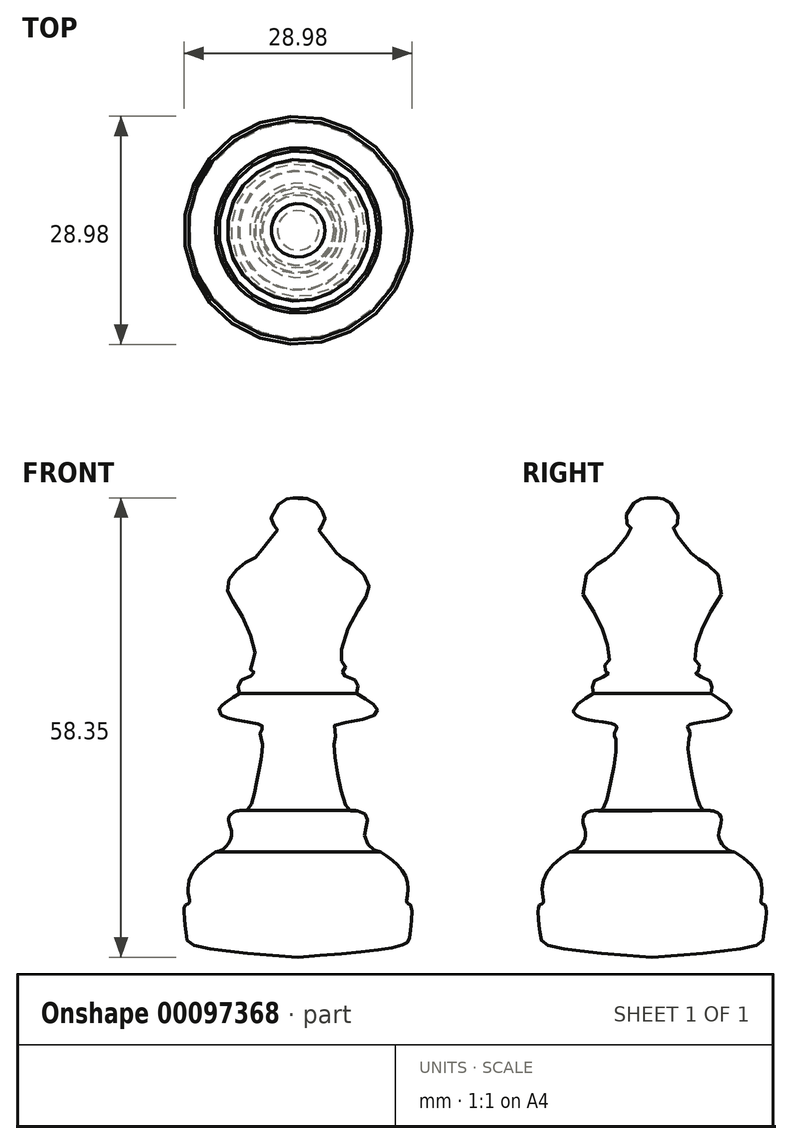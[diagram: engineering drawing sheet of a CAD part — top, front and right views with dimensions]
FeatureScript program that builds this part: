
annotation { "Feature Type Name" : "Feature", "Feature Type Description" : "" }
export const myFeature = defineFeature(function(context is Context, id is Id, definition is map)
    precondition{}
    {
        {
            var Q0;
            Q0=qCreatedBy(makeId("Front.planeOp"),FACE);
            var sketch = newSketch(context, id + "F0", { "sketchPlane" : qUnion([Q0])});
            skLineSegment(sketch, "E0", {"start": v(0, 0) * mm, "end": v(0, 25.12) * mm});
            skLineSegment(sketch, "E1", {"start": v(0, 0) * mm, "end": v(0, -33.17) * mm});
            skLineSegment(sketch, "E2", {"start": v(0, -33.17) * mm, "end": v(0.68, -33.17) * mm});
            skFitSpline(sketch, "E3", {"points": [v(0, 25.12) * mm, v(1.17, 25.12) * mm, v(2.58, 24.28) * mm, v(3.2, 23.27) * mm, v(3.4, 22.26) * mm, v(2.79, 21.45) * mm, v(2.58, 21.25) * mm, v(4.2, 19.13) * mm, v(5.32, 17.7) * mm, v(6.63, 17) * mm, v(8.75, 14.78) * mm, v(8.86, 13.06) * mm, v(6.93, 9.82) * mm, v(5.42, 4.66) * mm, v(5.82, 4.26) * mm, v(6.02, 3.35) * mm, v(5.62, 3.04) * mm, v(5.62, 2.74) * mm, v(6.83, 2.24) * mm, v(7.64, 1.53) * mm, v(7.54, 1.02) * mm, v(7.44, 0) * mm], "startDerivative": vector(25.38, 3.5) * mm, "endDerivative": vector(-0.86, -27) * mm});
            skFitSpline(sketch, "E4", {"points": [v(7.45, 0.37) * mm, v(9.46, -1) * mm, v(10.07, -1.81) * mm, v(8.86, -2.82) * mm, v(4.5, -3.83) * mm, v(4.8, -4.64) * mm, v(4.6, -5.55) * mm, v(5.01, -9.7) * mm, v(6.43, -14.45) * mm, v(7.45, -14.55) * mm, v(8.65, -15.16) * mm, v(8.75, -16.17) * mm, v(8.45, -17.79) * mm, v(9.46, -19.4) * mm, v(10.47, -19.81) * mm], "startDerivative": vector(26.98, -17.33) * mm, "endDerivative": vector(18.22, -4.06) * mm});
            skFitSpline(sketch, "E5", {"points": [v(10.47, -19.81) * mm, v(12.55, -21.35) * mm, v(13.77, -23.2) * mm, v(13.9, -25.35) * mm, v(13.84, -26.28) * mm, v(14.34, -26.57) * mm, v(14.2, -30.29) * mm, v(13.7, -31.43) * mm, v(0, -33.17) * mm], "startDerivative": vector(18.01, -11.72) * mm, "endDerivative": vector(-64.71, -4.87) * mm});
            skSolve(sketch);
        }
        {
            var Q0;
            Q0 = qSketchRegion(id + "F0", true);
            var Q1;
            Q1=sQuery(id+"F0.wireOp",EDGE,"E1");
            revolve(context, id + "F1", {"entities" : qUnion([Q0]), "axis" : qUnion([Q1]), "revolveType" : RevolveType.FULL});
        }
    });
